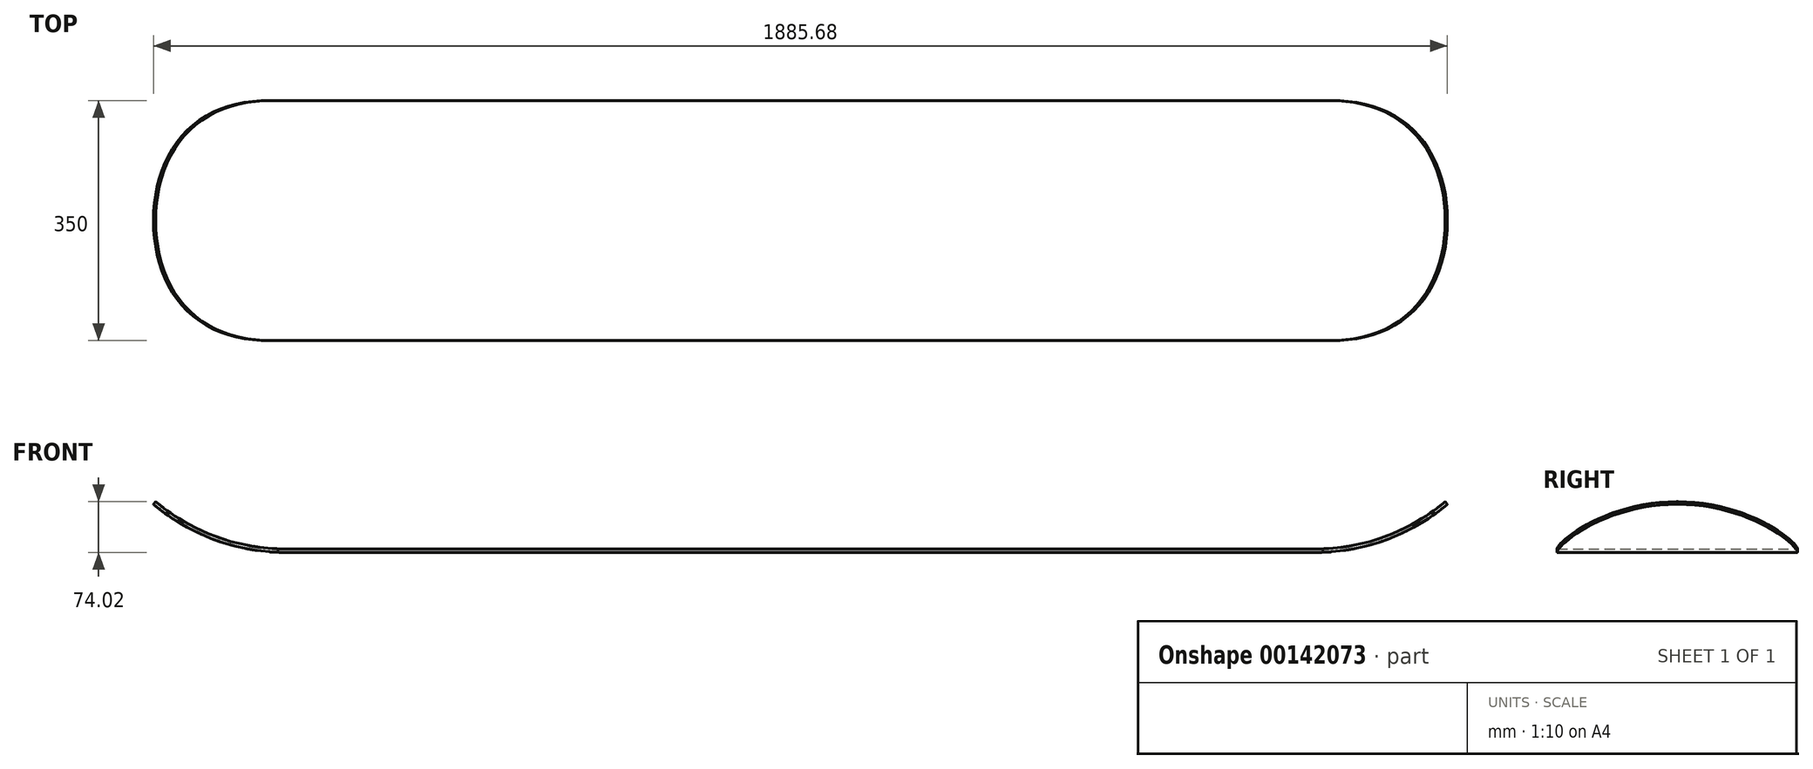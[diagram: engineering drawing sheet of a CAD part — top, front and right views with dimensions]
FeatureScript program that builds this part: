
annotation { "Feature Type Name" : "Feature", "Feature Type Description" : "" }
export const myFeature = defineFeature(function(context is Context, id is Id, definition is map)
    precondition{}
    {
        {
            var Q0;
            Q0=qCreatedBy(makeId("Front.planeOp"),FACE);
            var sketch = newSketch(context, id + "F0", { "sketchPlane" : qUnion([Q0])});
            skLineSegment(sketch, "E0", {"start": v(0, 0) * mm, "end": v(-750, 0) * mm});
            skArc(sketch, "E1", {"start": v(-942.84, 70.19) * mm, "mid": v(-852.6, 18.1) * mm, "end": v(-750, 0) * mm});
            skLineSegment(sketch, "E2", {"start": v(-942.84, 70.19) * mm, "end": v(-939.62, 74.02) * mm});
            skArc(sketch, "E3", {"start": v(-939.62, 74.02) * mm, "mid": v(-850.9, 22.8) * mm, "end": v(-750, 5) * mm});
            skLineSegment(sketch, "E4", {"start": v(-750, 5) * mm, "end": v(0, 5) * mm});
            skLineSegment(sketch, "E5", {"start": v(0, 5) * mm, "end": v(0, 0) * mm});
            skSolve(sketch);
        }
        {
            var Q0;
            Q0=makeQuery(id+"F0.imprint","IMPRINT",FACE,{"disambiguationData":[TD([[makeQuery(id+"F0.imprint","IMPRINT",EDGE,{"derivedFrom":sQuery(id+"F0.wireOp",EDGE,"E0")}),-1.0]])]});
            extrude(context, id + "F1", {"entities" : qUnion([Q0]), "endBound" : BoundingType.SYMMETRIC, "depth" : 350 * mm});
        }
        {
            var Q0;
            Q0=makeQuery(id+"F1.opExtrude","CAP_EDGE",EDGE,{"disambiguationData":[OSD([sQuery(id+"F0.wireOp",EDGE,"E2")])],"isStart":false});
            var Q1;
            Q1=makeQuery(id+"F1.opExtrude","CAP_EDGE",EDGE,{"disambiguationData":[OSD([sQuery(id+"F0.wireOp",EDGE,"E2")])],"isStart":true});
            fillet(context, id + "F2", {"entities" : qUnion([Q0, Q1]), "radius" : 174 * mm, "tangentPropagation" : true, "allowEdgeOverflow" : false});
        }
        {
            var Q0;
            Q0=makeQuery(id+"F1.opExtrude","SWEPT_BODY",BODY,{"disambiguationData":[OSD([sQuery(id+"F0.wireOp",EDGE,"E0"),sQuery(id+"F0.wireOp",EDGE,"E1"),sQuery(id+"F0.wireOp",EDGE,"E2"),sQuery(id+"F0.wireOp",EDGE,"E3"),sQuery(id+"F0.wireOp",EDGE,"E4"),sQuery(id+"F0.wireOp",EDGE,"E5")])]});
            var Q1;
            Q1=qCreatedBy(makeId("Right.planeOp"),FACE);
            mirror(context, id + "F3", {"operationType" : NewBodyOperationType.ADD, "entities" : qUnion([Q0]), "mirrorPlane" : qUnion([Q1])});
        }
    });
